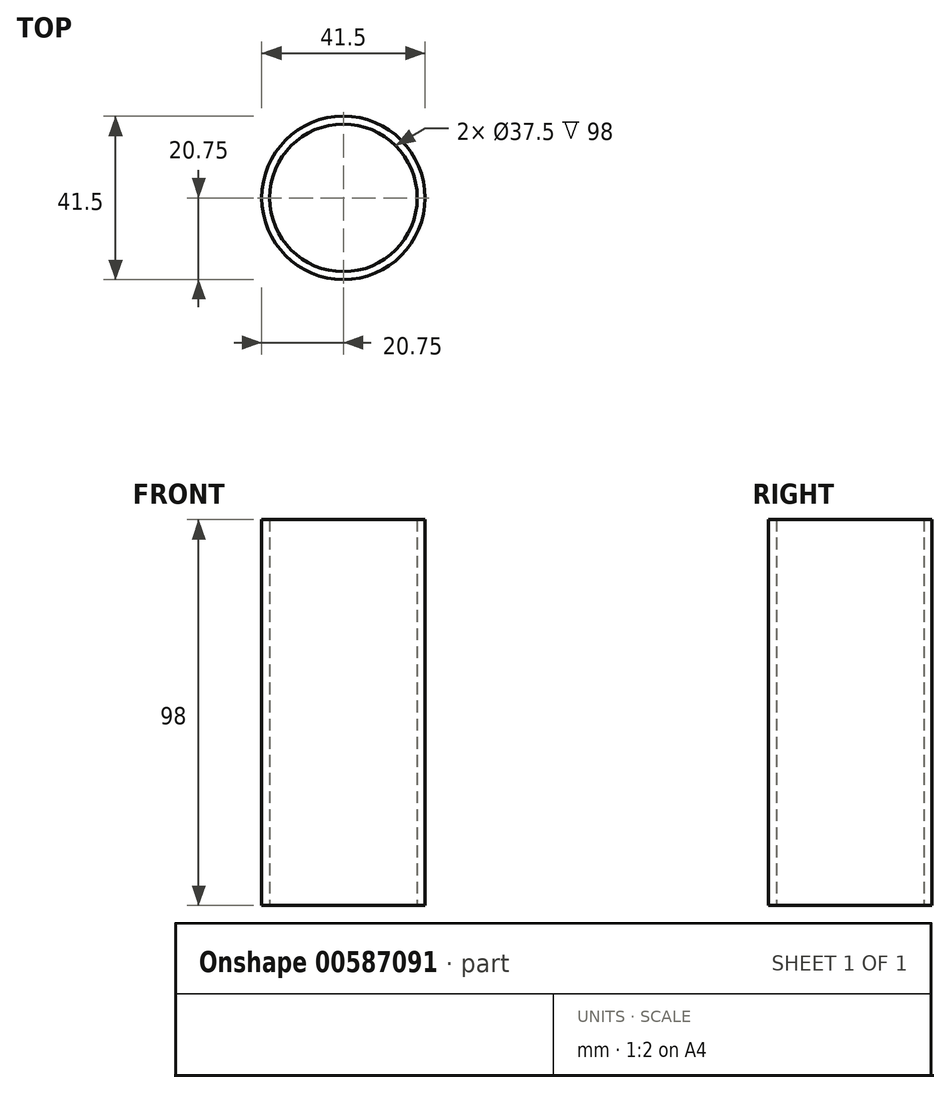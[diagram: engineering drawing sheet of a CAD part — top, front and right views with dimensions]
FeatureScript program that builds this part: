
annotation { "Feature Type Name" : "Feature", "Feature Type Description" : "" }
export const myFeature = defineFeature(function(context is Context, id is Id, definition is map)
    precondition{}
    {
        {
            var Q0;
            Q0=qCreatedBy(makeId("Top.planeOp"),FACE);
            var sketch = newSketch(context, id + "F0", { "sketchPlane" : qUnion([Q0])});
            skCircle(sketch, "E0", {"center": v(0, 0) * mm, "radius": 20.75 * mm});
            skCircle(sketch, "E1", {"center": v(0, 0) * mm, "radius": 18.75 * mm});
            skSolve(sketch);
        }
        {
            var Q0;
            Q0 = qSketchRegion(id + "F0", true);
            extrude(context, id + "F1", {"entities" : qUnion([Q0]), "depth" : 98 * mm, "offsetDistance" : 25 * mm});
        }
    });
